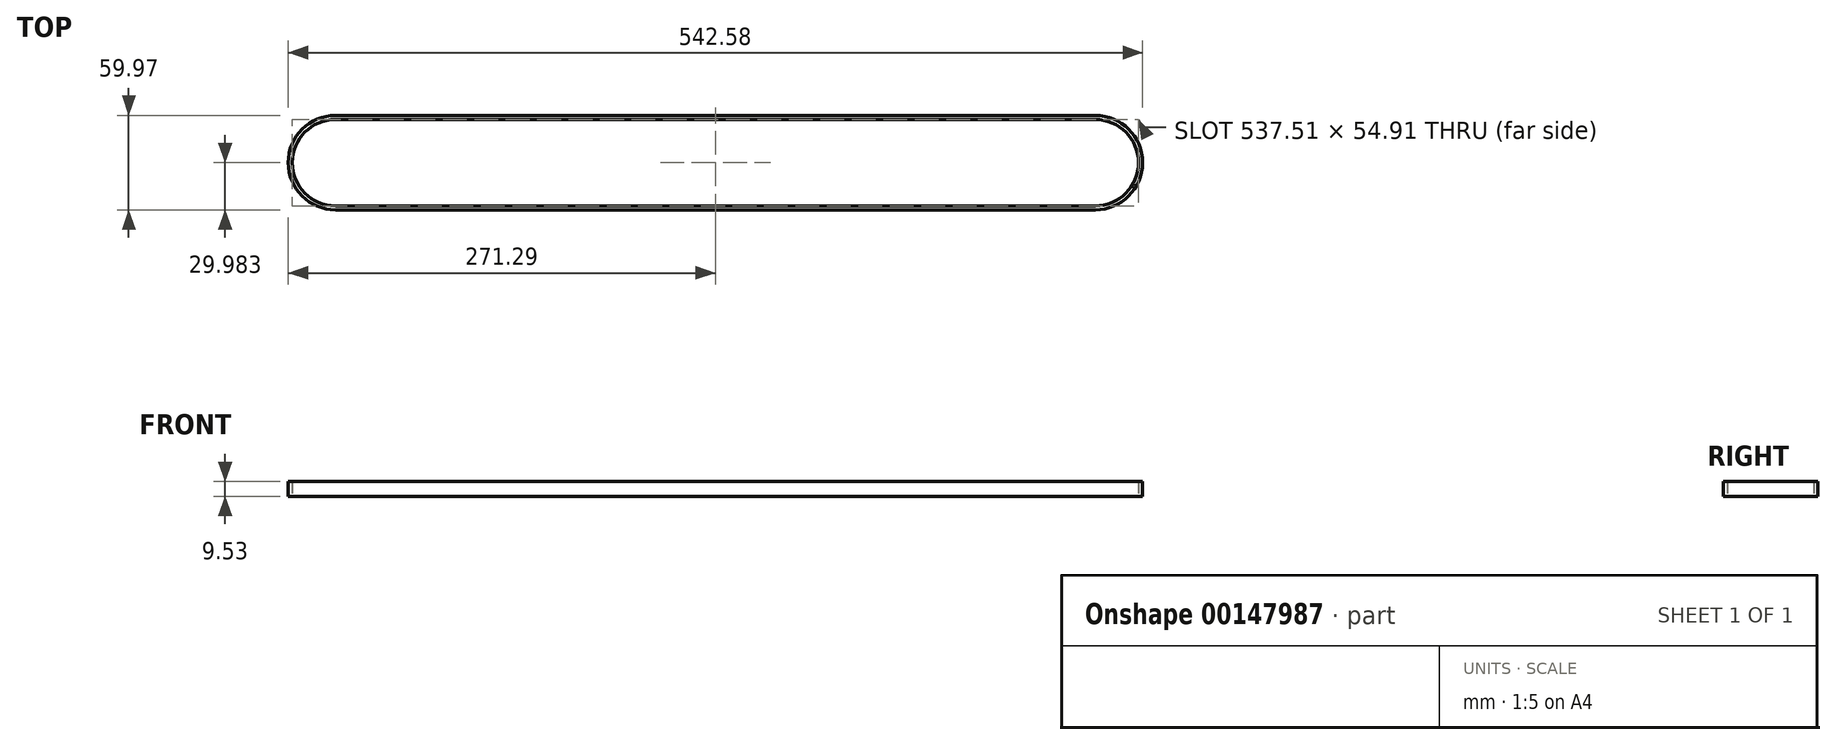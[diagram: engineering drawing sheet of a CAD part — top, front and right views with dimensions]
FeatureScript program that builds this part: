
annotation { "Feature Type Name" : "Feature", "Feature Type Description" : "" }
export const myFeature = defineFeature(function(context is Context, id is Id, definition is map)
    precondition{}
    {
        {
            var Q0;
            Q0=qCreatedBy(makeId("Top.planeOp"),FACE);
            var sketch = newSketch(context, id + "F0", { "sketchPlane" : qUnion([Q0])});
            skLineSegment(sketch, "E0.bottom", {"start": v(0, 0) * mm, "end": v(482.6, 0) * mm});
            skLineSegment(sketch, "E0.top", {"start": v(0, -2.53) * mm, "end": v(482.6, -2.53) * mm});
            skLineSegment(sketch, "E0.left", {"start": v(0, 0) * mm, "end": v(0, -2.53) * mm, "construction": true});
            skLineSegment(sketch, "E0.right", {"start": v(482.6, 0) * mm, "end": v(482.6, -2.53) * mm, "construction": true});
            skLineSegment(sketch, "E1", {"start": v(0, -2.53) * mm, "end": v(0, -57.44) * mm, "construction": true});
            skLineSegment(sketch, "E2", {"start": v(482.6, -2.53) * mm, "end": v(482.6, -57.44) * mm, "construction": true});
            skLineSegment(sketch, "E3.bottom", {"start": v(0, -57.44) * mm, "end": v(482.6, -57.44) * mm});
            skLineSegment(sketch, "E3.top", {"start": v(0, -59.97) * mm, "end": v(482.6, -59.97) * mm});
            skLineSegment(sketch, "E3.left", {"start": v(0, -57.44) * mm, "end": v(0, -59.97) * mm, "construction": true});
            skLineSegment(sketch, "E3.right", {"start": v(482.6, -57.44) * mm, "end": v(482.6, -59.97) * mm, "construction": true});
            skArc(sketch, "E4", {"start": v(482.6, -57.44) * mm, "mid": v(510.06, -29.99) * mm, "end": v(482.6, -2.53) * mm});
            skArc(sketch, "E5", {"start": v(482.6, -59.97) * mm, "mid": v(512.59, -29.99) * mm, "end": v(482.6, 0) * mm});
            skArc(sketch, "E6", {"start": v(0, -2.53) * mm, "mid": v(-27.46, -29.99) * mm, "end": v(0, -57.44) * mm});
            skArc(sketch, "E7", {"start": v(0, 0) * mm, "mid": v(-29.99, -29.99) * mm, "end": v(0, -59.97) * mm});
            skSolve(sketch);
        }
        {
            var Q0;
            Q0=qSketchRegion(id+"F0",true);
            extrude(context, id + "F1", {"entities" : qUnion([Q0]), "depth" : 9.52 * mm});
        }
    });
